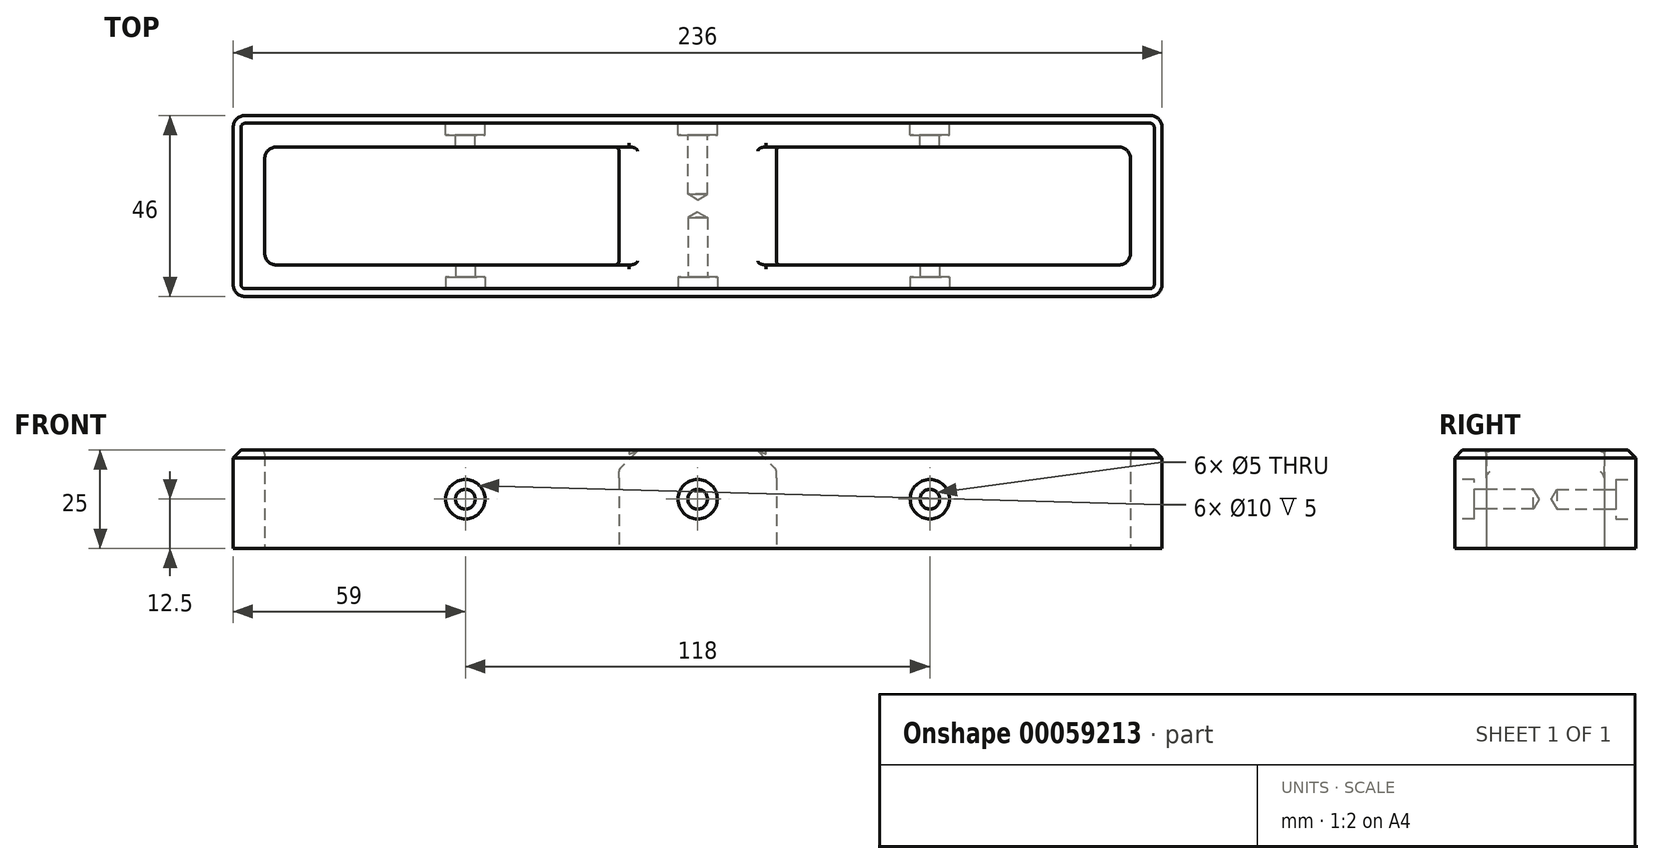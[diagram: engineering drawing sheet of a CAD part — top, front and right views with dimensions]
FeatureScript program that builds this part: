
annotation { "Feature Type Name" : "Feature", "Feature Type Description" : "" }
export const myFeature = defineFeature(function(context is Context, id is Id, definition is map)
    precondition{}
    {
        {
            var Q0;
            Q0=qCreatedBy(makeId("Top.planeOp"),FACE);
            var sketch = newSketch(context, id + "F0", { "sketchPlane" : qUnion([Q0])});
            skLineSegment(sketch, "E0.rect.bottom", {"start": v(115, 23) * mm, "end": v(-115, 23) * mm});
            skLineSegment(sketch, "E0.rect.top", {"start": v(115, -23) * mm, "end": v(-115, -23) * mm});
            skLineSegment(sketch, "E0.rect.left", {"start": v(118, 20) * mm, "end": v(118, -20) * mm});
            skLineSegment(sketch, "E0.rect.right", {"start": v(-118, 20) * mm, "end": v(-118, -20) * mm});
            skPoint(sketch, "E0.rect.middle", {"position": v(0, 0) * mm});
            skLineSegment(sketch, "E1.rect.bottom", {"start": v(107, -15) * mm, "end": v(20, -15) * mm});
            skLineSegment(sketch, "E1.rect.top", {"start": v(107, 15) * mm, "end": v(20, 15) * mm});
            skLineSegment(sketch, "E1.rect.left", {"start": v(110, -12) * mm, "end": v(110, 12) * mm});
            skLineSegment(sketch, "E1.rect.right", {"start": v(20, -15) * mm, "end": v(20, 15) * mm});
            skPoint(sketch, "E1.rect.middle", {"position": v(65, 0) * mm});
            skPoint(sketch, "E2.visualSharp", {"position": v(118, 23) * mm});
            skArc(sketch, "E2.filletArc", {"start": v(118, 20) * mm, "mid": v(117.12, 22.12) * mm, "end": v(115, 23) * mm});
            skPoint(sketch, "E3.visualSharp", {"position": v(118, -23) * mm});
            skArc(sketch, "E3.filletArc", {"start": v(115, -23) * mm, "mid": v(117.12, -22.12) * mm, "end": v(118, -20) * mm});
            skPoint(sketch, "E4.visualSharp", {"position": v(-118, -23) * mm});
            skArc(sketch, "E4.filletArc", {"start": v(-118, -20) * mm, "mid": v(-117.12, -22.12) * mm, "end": v(-115, -23) * mm});
            skPoint(sketch, "E5.visualSharp", {"position": v(-118, 23) * mm});
            skArc(sketch, "E5.filletArc", {"start": v(-115, 23) * mm, "mid": v(-117.12, 22.12) * mm, "end": v(-118, 20) * mm});
            skPoint(sketch, "E6.visualSharp", {"position": v(110, -15) * mm});
            skArc(sketch, "E6.filletArc", {"start": v(107, -15) * mm, "mid": v(109.12, -14.12) * mm, "end": v(110, -12) * mm});
            skPoint(sketch, "E7.visualSharp", {"position": v(110, 15) * mm});
            skArc(sketch, "E7.filletArc", {"start": v(110, 12) * mm, "mid": v(109.12, 14.12) * mm, "end": v(107, 15) * mm});
            skLineSegment(sketch, "E8", {"start": v(0, 0) * mm, "end": v(0, 91.6) * mm, "construction": true});
            skPoint(sketch, "E9.MirrorP", {"position": v(-110, 15) * mm});
            skArc(sketch, "E10.MirrorCS", {"start": v(-110, 12) * mm, "mid": v(-109.12, 14.12) * mm, "end": v(-107, 15) * mm});
            skPoint(sketch, "E11.MirrorP", {"position": v(-110, -15) * mm});
            skLineSegment(sketch, "E12.MirrorCS", {"start": v(-20, -15) * mm, "end": v(-20, 15) * mm});
            skLineSegment(sketch, "E13.MirrorCS", {"start": v(-110, -12) * mm, "end": v(-110, 12) * mm});
            skPoint(sketch, "E14.MirrorP", {"position": v(-65, 0) * mm});
            skLineSegment(sketch, "E15.MirrorCS", {"start": v(-107, 15) * mm, "end": v(-20, 15) * mm});
            skLineSegment(sketch, "E16.MirrorCS", {"start": v(-107, -15) * mm, "end": v(-20, -15) * mm});
            skArc(sketch, "E17.MirrorCS", {"start": v(-107, -15) * mm, "mid": v(-109.12, -14.12) * mm, "end": v(-110, -12) * mm});
            skSolve(sketch);
        }
        {
            var Q0;
            Q0=makeQuery(id+"F0.imprint","IMPRINT",FACE,{"disambiguationData":[TD([[makeQuery(id+"F0.imprint","IMPRINT",EDGE,{"derivedFrom":sQuery(id+"F0.wireOp",EDGE,"E0.rect.bottom")}),1.0]])]});
            extrude(context, id + "F1", {"entities" : qUnion([Q0]), "depth" : 25 * mm});
        }
        {
            var Q0;
            Q0=makeQuery(id+"F1.opExtrude","CAP_EDGE",EDGE,{"disambiguationData":[OSD([sQuery(id+"F0.wireOp",EDGE,"E0.rect.bottom")])],"isStart":false});
            chamfer(context, id + "F2", {"entities" : qUnion([Q0]), "width" : 2 * mm, "tangentPropagation" : true});
        }
        {
            var Q0;
            Q0=makeQuery(id+"F1.opExtrude","CAP_EDGE",EDGE,{"disambiguationData":[OSD([sQuery(id+"F0.wireOp",EDGE,"E1.rect.right")])],"isStart":false});
            var Q1;
            Q1=makeQuery(id+"F1.opExtrude","CAP_EDGE",EDGE,{"disambiguationData":[OSD([sQuery(id+"F0.wireOp",EDGE,"E12.MirrorCS")])],"isStart":false});
            chamfer(context, id + "F3", {"entities" : qUnion([Q0, Q1]), "width" : 5 * mm});
        }
        {
            var Q0;
            Q0=makeQuery(id+"F1.opExtrude","SWEPT_FACE",FACE,{"disambiguationData":[OSD([sQuery(id+"F0.wireOp",EDGE,"E0.rect.top")])]});
            var sketch = newSketch(context, id + "F4", { "sketchPlane" : qUnion([Q0])});
            skLineSegment(sketch, "E18", {"start": v(0, 0) * mm, "end": v(0, 25) * mm, "construction": true});
            skPoint(sketch, "E19", {"position": v(0, 12.5) * mm});
            skLineSegment(sketch, "E20", {"start": v(0, 12.5) * mm, "end": v(-118, 12.5) * mm, "construction": true});
            skLineSegment(sketch, "E21", {"start": v(0, 12.5) * mm, "end": v(118, 12.5) * mm, "construction": true});
            skPoint(sketch, "E22", {"position": v(59, 12.5) * mm});
            skPoint(sketch, "E23", {"position": v(-59, 12.5) * mm});
            skSolve(sketch);
        }
        {
            var Q0;
            Q0=sQuery(id+"F4.wireOp",VERTEX,"E23");
            var Q1;
            Q1=sQuery(id+"F4.wireOp",VERTEX,"E22");
            var Q2;
            Q2=sQuery(id+"F4.wireOp",VERTEX,"E19");
            var Q3;
            Q3=makeQuery(id+"F1.opExtrude","SWEPT_BODY",BODY,{"disambiguationData":[OSD([sQuery(id+"F0.wireOp",EDGE,"E0.rect.bottom"),sQuery(id+"F0.wireOp",EDGE,"E0.rect.top"),sQuery(id+"F0.wireOp",EDGE,"E0.rect.left"),sQuery(id+"F0.wireOp",EDGE,"E0.rect.right"),sQuery(id+"F0.wireOp",EDGE,"E1.rect.bottom"),sQuery(id+"F0.wireOp",EDGE,"E1.rect.top"),sQuery(id+"F0.wireOp",EDGE,"E1.rect.left"),sQuery(id+"F0.wireOp",EDGE,"E1.rect.right"),sQuery(id+"F0.wireOp",EDGE,"E2.filletArc"),sQuery(id+"F0.wireOp",EDGE,"E3.filletArc"),sQuery(id+"F0.wireOp",EDGE,"E4.filletArc"),sQuery(id+"F0.wireOp",EDGE,"E5.filletArc"),sQuery(id+"F0.wireOp",EDGE,"E6.filletArc"),sQuery(id+"F0.wireOp",EDGE,"E7.filletArc"),sQuery(id+"F0.wireOp",EDGE,"E10.MirrorCS"),sQuery(id+"F0.wireOp",EDGE,"E12.MirrorCS"),sQuery(id+"F0.wireOp",EDGE,"E13.MirrorCS"),sQuery(id+"F0.wireOp",EDGE,"E15.MirrorCS"),sQuery(id+"F0.wireOp",EDGE,"E16.MirrorCS"),sQuery(id+"F0.wireOp",EDGE,"E17.MirrorCS")])]});
            hole(context, id + "F5", {"style" : HoleStyle.C_BORE, "holeDiameter" : 5 * mm, "cBoreDiameter" : 10 * mm, "cBoreDepth" : 5 * mm, "endStyle" : HoleEndStyle.BLIND, "holeDepth" : 20 * mm, "locations" : qUnion([Q0, Q1, Q2]), "scope" : qUnion([Q3])});
        }
        {
            var Q0;
            Q0=makeQuery(id+"F1.opExtrude","CAP_EDGE",EDGE,{"disambiguationData":[OSD([sQuery(id+"F0.wireOp",EDGE,"E15.MirrorCS")])],"isStart":false});
            var Q1;
            Q1=makeQuery(id+"F1.opExtrude","CAP_EDGE",EDGE,{"disambiguationData":[OSD([sQuery(id+"F0.wireOp",EDGE,"E1.rect.top")])],"isStart":false});
            var Q2;
            {var subQ0=sQuery(id+"F0.wireOp",EDGE,"E1.rect.right");Q2=makeQuery(id+"F3.opChamfer","BLEND_EDGE",EDGE,{"blendedFrom":[makeQuery(id+"F1.opExtrude","CAP_EDGE",EDGE,{"disambiguationData":[OSD([subQ0])],"isStart":false}),makeQuery(id+"F1.opExtrude","SWEPT_FACE",FACE,{"disambiguationData":[OSD([subQ0])]})],"blendedInto":[makeQuery(id+"F1.opExtrude","SWEPT_FACE",FACE,{"disambiguationData":[OSD([subQ0])]})]});}
            var Q3;
            {var subQ0=sQuery(id+"F0.wireOp",EDGE,"E12.MirrorCS");Q3=makeQuery(id+"F3.opChamfer","BLEND_EDGE",EDGE,{"blendedFrom":[makeQuery(id+"F1.opExtrude","CAP_EDGE",EDGE,{"disambiguationData":[OSD([subQ0])],"isStart":false}),makeQuery(id+"F1.opExtrude","SWEPT_FACE",FACE,{"disambiguationData":[OSD([subQ0])]})],"blendedInto":[makeQuery(id+"F1.opExtrude","SWEPT_FACE",FACE,{"disambiguationData":[OSD([subQ0])]})]});}
            var Q4;
            {var subQ0=sQuery(id+"F0.wireOp",EDGE,"E12.MirrorCS");Q4=makeQuery(id+"F3.opChamfer","BLEND_EDGE",EDGE,{"blendedFrom":[makeQuery(id+"F1.opExtrude","CAP_EDGE",EDGE,{"disambiguationData":[OSD([subQ0])],"isStart":false}),makeQuery(id+"F1.opExtrude","CAP_FACE",FACE,{"disambiguationData":[OSD([sQuery(id+"F0.wireOp",EDGE,"E0.rect.bottom"),sQuery(id+"F0.wireOp",EDGE,"E0.rect.top"),sQuery(id+"F0.wireOp",EDGE,"E0.rect.left"),sQuery(id+"F0.wireOp",EDGE,"E0.rect.right"),sQuery(id+"F0.wireOp",EDGE,"E1.rect.bottom"),sQuery(id+"F0.wireOp",EDGE,"E1.rect.top"),sQuery(id+"F0.wireOp",EDGE,"E1.rect.left"),sQuery(id+"F0.wireOp",EDGE,"E1.rect.right"),sQuery(id+"F0.wireOp",EDGE,"E2.filletArc"),sQuery(id+"F0.wireOp",EDGE,"E3.filletArc"),sQuery(id+"F0.wireOp",EDGE,"E4.filletArc"),sQuery(id+"F0.wireOp",EDGE,"E5.filletArc"),sQuery(id+"F0.wireOp",EDGE,"E6.filletArc"),sQuery(id+"F0.wireOp",EDGE,"E7.filletArc"),sQuery(id+"F0.wireOp",EDGE,"E10.MirrorCS"),subQ0,sQuery(id+"F0.wireOp",EDGE,"E13.MirrorCS"),sQuery(id+"F0.wireOp",EDGE,"E15.MirrorCS"),sQuery(id+"F0.wireOp",EDGE,"E16.MirrorCS"),sQuery(id+"F0.wireOp",EDGE,"E17.MirrorCS")])],"isStart":false})],"blendedInto":[makeQuery(id+"F1.opExtrude","CAP_FACE",FACE,{"disambiguationData":[OSD([sQuery(id+"F0.wireOp",EDGE,"E0.rect.bottom"),sQuery(id+"F0.wireOp",EDGE,"E0.rect.top"),sQuery(id+"F0.wireOp",EDGE,"E0.rect.left"),sQuery(id+"F0.wireOp",EDGE,"E0.rect.right"),sQuery(id+"F0.wireOp",EDGE,"E1.rect.bottom"),sQuery(id+"F0.wireOp",EDGE,"E1.rect.top"),sQuery(id+"F0.wireOp",EDGE,"E1.rect.left"),sQuery(id+"F0.wireOp",EDGE,"E1.rect.right"),sQuery(id+"F0.wireOp",EDGE,"E2.filletArc"),sQuery(id+"F0.wireOp",EDGE,"E3.filletArc"),sQuery(id+"F0.wireOp",EDGE,"E4.filletArc"),sQuery(id+"F0.wireOp",EDGE,"E5.filletArc"),sQuery(id+"F0.wireOp",EDGE,"E6.filletArc"),sQuery(id+"F0.wireOp",EDGE,"E7.filletArc"),sQuery(id+"F0.wireOp",EDGE,"E10.MirrorCS"),subQ0,sQuery(id+"F0.wireOp",EDGE,"E13.MirrorCS"),sQuery(id+"F0.wireOp",EDGE,"E15.MirrorCS"),sQuery(id+"F0.wireOp",EDGE,"E16.MirrorCS"),sQuery(id+"F0.wireOp",EDGE,"E17.MirrorCS")])],"isStart":false})]});}
            var Q5;
            {var subQ0=sQuery(id+"F0.wireOp",EDGE,"E1.rect.right");Q5=makeQuery(id+"F3.opChamfer","BLEND_EDGE",EDGE,{"blendedFrom":[makeQuery(id+"F1.opExtrude","CAP_EDGE",EDGE,{"disambiguationData":[OSD([subQ0])],"isStart":false}),makeQuery(id+"F1.opExtrude","CAP_FACE",FACE,{"disambiguationData":[OSD([sQuery(id+"F0.wireOp",EDGE,"E0.rect.bottom"),sQuery(id+"F0.wireOp",EDGE,"E0.rect.top"),sQuery(id+"F0.wireOp",EDGE,"E0.rect.left"),sQuery(id+"F0.wireOp",EDGE,"E0.rect.right"),sQuery(id+"F0.wireOp",EDGE,"E1.rect.bottom"),sQuery(id+"F0.wireOp",EDGE,"E1.rect.top"),sQuery(id+"F0.wireOp",EDGE,"E1.rect.left"),subQ0,sQuery(id+"F0.wireOp",EDGE,"E2.filletArc"),sQuery(id+"F0.wireOp",EDGE,"E3.filletArc"),sQuery(id+"F0.wireOp",EDGE,"E4.filletArc"),sQuery(id+"F0.wireOp",EDGE,"E5.filletArc"),sQuery(id+"F0.wireOp",EDGE,"E6.filletArc"),sQuery(id+"F0.wireOp",EDGE,"E7.filletArc"),sQuery(id+"F0.wireOp",EDGE,"E10.MirrorCS"),sQuery(id+"F0.wireOp",EDGE,"E12.MirrorCS"),sQuery(id+"F0.wireOp",EDGE,"E13.MirrorCS"),sQuery(id+"F0.wireOp",EDGE,"E15.MirrorCS"),sQuery(id+"F0.wireOp",EDGE,"E16.MirrorCS"),sQuery(id+"F0.wireOp",EDGE,"E17.MirrorCS")])],"isStart":false})],"blendedInto":[makeQuery(id+"F1.opExtrude","CAP_FACE",FACE,{"disambiguationData":[OSD([sQuery(id+"F0.wireOp",EDGE,"E0.rect.bottom"),sQuery(id+"F0.wireOp",EDGE,"E0.rect.top"),sQuery(id+"F0.wireOp",EDGE,"E0.rect.left"),sQuery(id+"F0.wireOp",EDGE,"E0.rect.right"),sQuery(id+"F0.wireOp",EDGE,"E1.rect.bottom"),sQuery(id+"F0.wireOp",EDGE,"E1.rect.top"),sQuery(id+"F0.wireOp",EDGE,"E1.rect.left"),subQ0,sQuery(id+"F0.wireOp",EDGE,"E2.filletArc"),sQuery(id+"F0.wireOp",EDGE,"E3.filletArc"),sQuery(id+"F0.wireOp",EDGE,"E4.filletArc"),sQuery(id+"F0.wireOp",EDGE,"E5.filletArc"),sQuery(id+"F0.wireOp",EDGE,"E6.filletArc"),sQuery(id+"F0.wireOp",EDGE,"E7.filletArc"),sQuery(id+"F0.wireOp",EDGE,"E10.MirrorCS"),sQuery(id+"F0.wireOp",EDGE,"E12.MirrorCS"),sQuery(id+"F0.wireOp",EDGE,"E13.MirrorCS"),sQuery(id+"F0.wireOp",EDGE,"E15.MirrorCS"),sQuery(id+"F0.wireOp",EDGE,"E16.MirrorCS"),sQuery(id+"F0.wireOp",EDGE,"E17.MirrorCS")])],"isStart":false})]});}
            var Q6;
            Q6=makeQuery(id+"F3.opChamfer","BLEND_EDGE",EDGE,{"blendedFrom":[makeQuery(id+"F1.opExtrude","CAP_EDGE",EDGE,{"disambiguationData":[OSD([sQuery(id+"F0.wireOp",EDGE,"E12.MirrorCS")])],"isStart":false}),makeQuery(id+"F1.opExtrude","SWEPT_FACE",FACE,{"disambiguationData":[OSD([sQuery(id+"F0.wireOp",EDGE,"E15.MirrorCS")])]})],"blendedInto":[makeQuery(id+"F1.opExtrude","SWEPT_FACE",FACE,{"disambiguationData":[OSD([sQuery(id+"F0.wireOp",EDGE,"E15.MirrorCS")])]})]});
            var Q7;
            Q7=makeQuery(id+"F3.opChamfer","BLEND_EDGE",EDGE,{"blendedFrom":[makeQuery(id+"F1.opExtrude","CAP_EDGE",EDGE,{"disambiguationData":[OSD([sQuery(id+"F0.wireOp",EDGE,"E12.MirrorCS")])],"isStart":false}),makeQuery(id+"F1.opExtrude","SWEPT_FACE",FACE,{"disambiguationData":[OSD([sQuery(id+"F0.wireOp",EDGE,"E16.MirrorCS")])]})],"blendedInto":[makeQuery(id+"F1.opExtrude","SWEPT_FACE",FACE,{"disambiguationData":[OSD([sQuery(id+"F0.wireOp",EDGE,"E16.MirrorCS")])]})]});
            var Q8;
            Q8=makeQuery(id+"F3.opChamfer","BLEND_EDGE",EDGE,{"blendedFrom":[makeQuery(id+"F1.opExtrude","CAP_EDGE",EDGE,{"disambiguationData":[OSD([sQuery(id+"F0.wireOp",EDGE,"E1.rect.right")])],"isStart":false}),makeQuery(id+"F1.opExtrude","SWEPT_FACE",FACE,{"disambiguationData":[OSD([sQuery(id+"F0.wireOp",EDGE,"E1.rect.top")])]})],"blendedInto":[makeQuery(id+"F1.opExtrude","SWEPT_FACE",FACE,{"disambiguationData":[OSD([sQuery(id+"F0.wireOp",EDGE,"E1.rect.top")])]})]});
            var Q9;
            Q9=makeQuery(id+"F3.opChamfer","BLEND_EDGE",EDGE,{"blendedFrom":[makeQuery(id+"F1.opExtrude","CAP_EDGE",EDGE,{"disambiguationData":[OSD([sQuery(id+"F0.wireOp",EDGE,"E1.rect.right")])],"isStart":false}),makeQuery(id+"F1.opExtrude","SWEPT_FACE",FACE,{"disambiguationData":[OSD([sQuery(id+"F0.wireOp",EDGE,"E1.rect.bottom")])]})],"blendedInto":[makeQuery(id+"F1.opExtrude","SWEPT_FACE",FACE,{"disambiguationData":[OSD([sQuery(id+"F0.wireOp",EDGE,"E1.rect.bottom")])]})]});
            fillet(context, id + "F6", {"entities" : qUnion([Q0, Q1, Q2, Q3, Q4, Q5, Q6, Q7, Q8, Q9]), "radius" : 1 * mm, "tangentPropagation" : true, "allowEdgeOverflow" : false});
        }
        {
            var Q0;
            Q0=makeQuery(id+"F1.opExtrude","SWEPT_FACE",FACE,{"disambiguationData":[OSD([sQuery(id+"F0.wireOp",EDGE,"E0.rect.bottom")])]});
            var sketch = newSketch(context, id + "F7", { "sketchPlane" : qUnion([Q0])});
            skPoint(sketch, "E24.0", {"position": v(-59, 12.5) * mm});
            skPoint(sketch, "E24.1", {"position": v(0, 12.5) * mm});
            skPoint(sketch, "E24.2", {"position": v(59, 12.5) * mm});
            skSolve(sketch);
        }
        {
            var Q0;
            Q0=sQuery(id+"F7.wireOp",VERTEX,"E24.0");
            var Q1;
            Q1=sQuery(id+"F7.wireOp",VERTEX,"E24.1");
            var Q2;
            Q2=sQuery(id+"F7.wireOp",VERTEX,"E24.2");
            var Q3;
            Q3=makeQuery(id+"F1.opExtrude","SWEPT_BODY",BODY,{"disambiguationData":[OSD([sQuery(id+"F0.wireOp",EDGE,"E0.rect.bottom"),sQuery(id+"F0.wireOp",EDGE,"E0.rect.top"),sQuery(id+"F0.wireOp",EDGE,"E0.rect.left"),sQuery(id+"F0.wireOp",EDGE,"E0.rect.right"),sQuery(id+"F0.wireOp",EDGE,"E1.rect.bottom"),sQuery(id+"F0.wireOp",EDGE,"E1.rect.top"),sQuery(id+"F0.wireOp",EDGE,"E1.rect.left"),sQuery(id+"F0.wireOp",EDGE,"E1.rect.right"),sQuery(id+"F0.wireOp",EDGE,"E2.filletArc"),sQuery(id+"F0.wireOp",EDGE,"E3.filletArc"),sQuery(id+"F0.wireOp",EDGE,"E4.filletArc"),sQuery(id+"F0.wireOp",EDGE,"E5.filletArc"),sQuery(id+"F0.wireOp",EDGE,"E6.filletArc"),sQuery(id+"F0.wireOp",EDGE,"E7.filletArc"),sQuery(id+"F0.wireOp",EDGE,"E10.MirrorCS"),sQuery(id+"F0.wireOp",EDGE,"E12.MirrorCS"),sQuery(id+"F0.wireOp",EDGE,"E13.MirrorCS"),sQuery(id+"F0.wireOp",EDGE,"E15.MirrorCS"),sQuery(id+"F0.wireOp",EDGE,"E16.MirrorCS"),sQuery(id+"F0.wireOp",EDGE,"E17.MirrorCS")])]});
            hole(context, id + "F8", {"style" : HoleStyle.C_BORE, "holeDiameter" : 5 * mm, "cBoreDiameter" : 10 * mm, "cBoreDepth" : 5 * mm, "endStyle" : HoleEndStyle.BLIND, "holeDepth" : 20 * mm, "locations" : qUnion([Q0, Q1, Q2]), "scope" : qUnion([Q3])});
        }
    });
